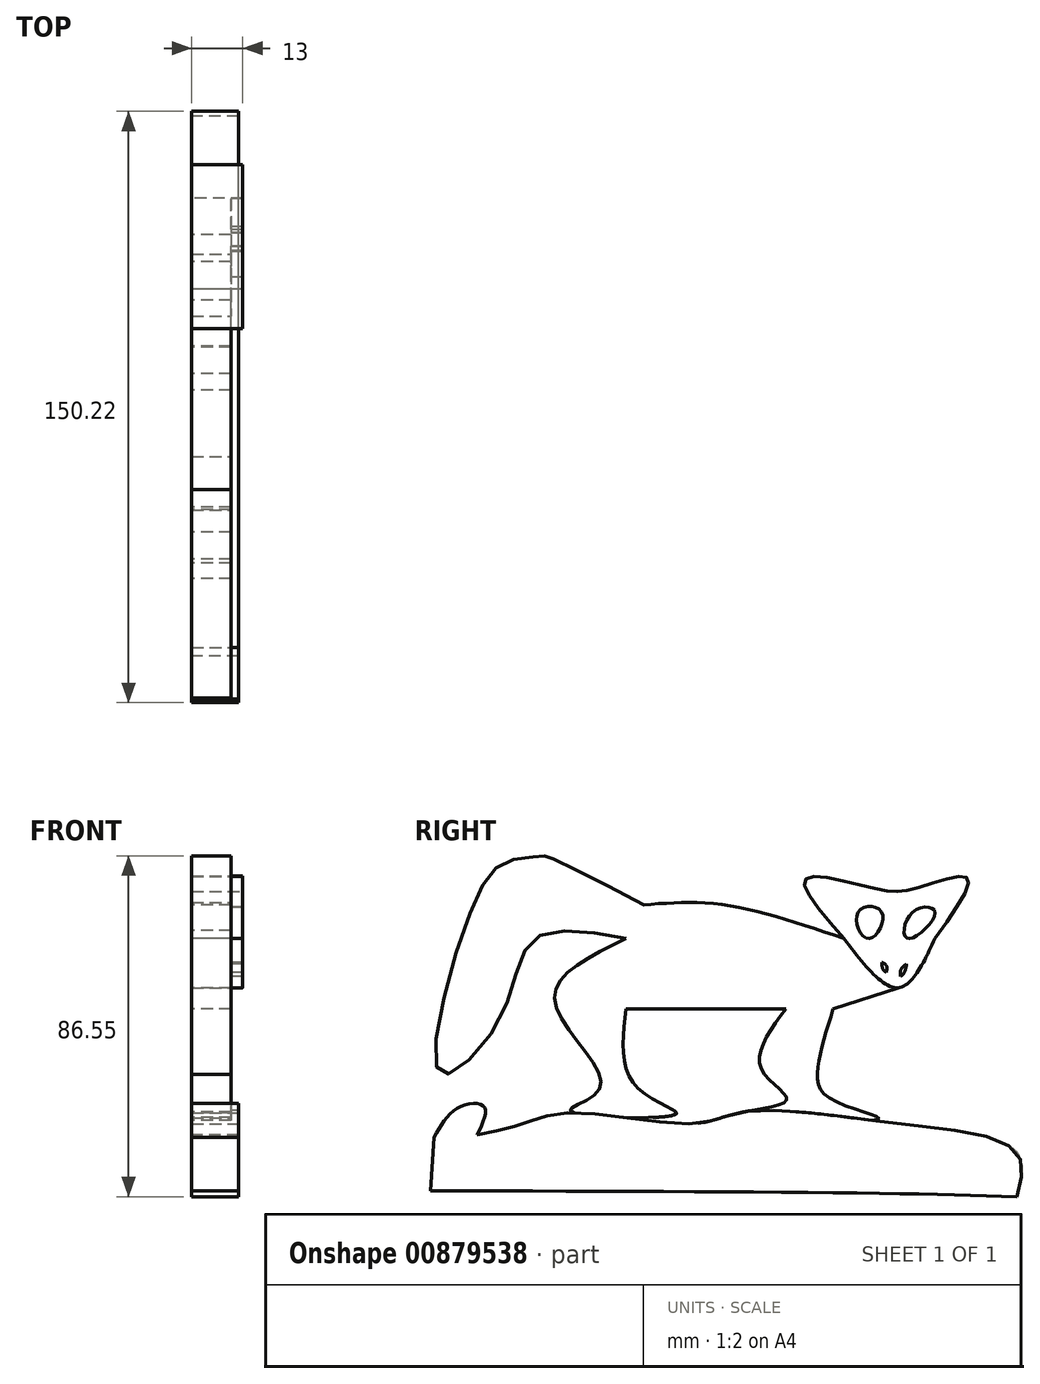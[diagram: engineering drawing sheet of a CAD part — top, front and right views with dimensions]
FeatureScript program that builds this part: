
annotation { "Feature Type Name" : "Feature", "Feature Type Description" : "" }
export const myFeature = defineFeature(function(context is Context, id is Id, definition is map)
    precondition{}
    {
        {
            var Q0;
            Q0=qCreatedBy(makeId("Right.planeOp"),FACE);
            var sketch = newSketch(context, id + "F0", { "sketchPlane" : qUnion([Q0])});
            skFitSpline(sketch, "E0", {"points": [v(-20.3, 8.57) * mm, v(-44.97, 20.9) * mm, v(-45.87, 20.9) * mm, v(-54.6, 19.7) * mm, v(-64.82, 5.56) * mm, v(-72.04, -34.14) * mm, v(-56.7, -20) * mm, v(-47.98, 0) * mm, v(-24.82, 0) * mm], "startDerivative": vector(-211.97, 110.73) * mm, "endDerivative": vector(178.69, -36.3) * mm});
            skFitSpline(sketch, "E1", {"points": [v(-24.82, 0) * mm, v(-42.86, -16.1) * mm, v(-31.43, -38.05) * mm, v(-38.95, -43.76) * mm, v(-12.18, -44.67) * mm, v(-21.8, -38.05) * mm, v(-24.82, -17.9) * mm], "startDerivative": vector(-149.38, -72.74) * mm, "endDerivative": vector(12.7, 128.41) * mm});
            skFitSpline(sketch, "E2", {"points": [v(-20.3, 8.57) * mm, v(0, 8.57) * mm, v(30.53, 0) * mm], "startDerivative": vector(43.61, 3.43) * mm, "endDerivative": vector(57.54, -19.72) * mm});
            skFitSpline(sketch, "E3", {"points": [v(-24.82, -17.9) * mm, v(-15.8, -17.9) * mm, v(3.76, -17.9) * mm, v(15.8, -17.9) * mm], "startDerivative": vector(28.68, 0) * mm, "endDerivative": vector(34.2, 0) * mm});
            skFitSpline(sketch, "E4", {"points": [v(15.8, -17.9) * mm, v(9.78, -33.54) * mm, v(15.8, -41.36) * mm, v(4.36, -44.37) * mm, v(39.25, -45.87) * mm, v(27.22, -40.76) * mm, v(23.91, -32.94) * mm, v(27.82, -17.9) * mm], "startDerivative": vector(-83.07, -110.92) * mm, "endDerivative": vector(34.72, 110.67) * mm});
            skFitSpline(sketch, "E5", {"points": [v(30.53, 0) * mm, v(20.9, 15.19) * mm, v(38.05, 12.78) * mm, v(48.88, 12.78) * mm, v(61.81, 15.5) * mm, v(53.7, 0) * mm], "startDerivative": vector(-80.15, 92.19) * mm, "endDerivative": vector(-69.87, -97.65) * mm});
            skFitSpline(sketch, "E6", {"points": [v(53.7, 0) * mm, v(44.37, -12.48) * mm, v(30.53, 0) * mm], "startDerivative": vector(-17.86, -38.08) * mm, "endDerivative": vector(-28.3, 36.96) * mm});
            skFitSpline(sketch, "E7", {"points": [v(44.37, -12.48) * mm, v(27.82, -17.9) * mm], "startDerivative": vector(-16.54, -5.41) * mm, "endDerivative": vector(-16.54, -5.41) * mm});
            skFitSpline(sketch, "E8", {"points": [v(34.14, 6.68) * mm, v(36.85, 0) * mm, v(40.16, 6.68) * mm, v(34.14, 6.68) * mm]});
            skFitSpline(sketch, "E9", {"points": [v(47.98, 6.68) * mm, v(46.77, 0) * mm, v(53.7, 6.68) * mm, v(47.98, 6.68) * mm]});
            skFitSpline(sketch, "E10", {"points": [v(40.16, -6.06) * mm, v(41.36, -8.57) * mm], "startDerivative": vector(1.2, -2.5) * mm, "endDerivative": vector(1.2, -2.5) * mm});
            skFitSpline(sketch, "E11", {"points": [v(46.47, -6.47) * mm, v(44.97, -9.17) * mm], "startDerivative": vector(-1.5, -2.7) * mm, "endDerivative": vector(-1.5, -2.7) * mm});
            skFitSpline(sketch, "E12", {"points": [v(40.16, -6.06) * mm, v(41.34, -6.9) * mm, v(41.36, -8.57) * mm], "startDerivative": vector(3.05, -1.37) * mm, "endDerivative": vector(-0.6, -3.62) * mm});
            skFitSpline(sketch, "E13", {"points": [v(46.47, -6.47) * mm, v(45.07, -7.74) * mm, v(44.97, -9.6) * mm], "startDerivative": vector(-3.45, -2.23) * mm, "endDerivative": vector(0.44, -4.06) * mm});
            skFitSpline(sketch, "E14", {"points": [v(46.47, -6.47) * mm, v(45.91, -8.57) * mm, v(44.97, -9.6) * mm], "startDerivative": vector(-0.7, -4.2) * mm, "endDerivative": vector(-2.37, -2) * mm});
            skFitSpline(sketch, "E15", {"points": [v(40.16, -6.06) * mm, v(40.56, -7.95) * mm, v(41.36, -8.57) * mm], "startDerivative": vector(0.34, -3.77) * mm, "endDerivative": vector(2.16, -1.11) * mm});
            skSolve(sketch);
        }
        {
            var Q0;
            Q0=makeQuery(id+"F0.imprint","IMPRINT",FACE,{"disambiguationData":[TD([[makeQuery(id+"F0.imprint","IMPRINT",EDGE,{"derivedFrom":sQuery(id+"F0.wireOp",EDGE,"E0")}),1.0]])]});
            extrude(context, id + "F1", {"entities" : qUnion([Q0]), "depth" : 10 * mm, "offsetDistance" : 25.4 * mm});
        }
        {
            var Q0;
            {var subQ1=sQuery(id+"F0.wireOp",EDGE,"E5");Q0=makeQuery(id+"F0.imprint","IMPRINT",FACE,{"disambiguationData":[TD([[makeQuery(id+"F0.imprint","IMPRINT",EDGE,{"derivedFrom":subQ1}),-1.0]])]});}
            extrude(context, id + "F2", {"entities" : qUnion([Q0]), "depth" : 13 * mm, "offsetDistance" : 25 * mm});
        }
        {
            var Q0;
            Q0=makeQuery(id+"F0.imprint","IMPRINT",FACE,{"disambiguationData":[TD([[makeQuery(id+"F0.imprint","IMPRINT",EDGE,{"derivedFrom":sQuery(id+"F0.wireOp",EDGE,"E8")}),1.0]])]});
            var Q1;
            Q1=makeQuery(id+"F0.imprint","IMPRINT",FACE,{"disambiguationData":[TD([[makeQuery(id+"F0.imprint","IMPRINT",EDGE,{"derivedFrom":sQuery(id+"F0.wireOp",EDGE,"E9")}),1.0]])]});
            extrude(context, id + "F3", {"entities" : qUnion([Q0, Q1]), "operationType" : NewBodyOperationType.ADD, "depth" : 10 * mm, "offsetDistance" : 25 * mm});
        }
        {
            var Q0;
            Q0=qCreatedBy(makeId("Right.planeOp"),FACE);
            var sketch = newSketch(context, id + "F4", { "sketchPlane" : qUnion([Q0])});
            skFitSpline(sketch, "E16", {"points": [v(-74.46, -64.1) * mm, v(37.15, -64.69) * mm, v(74.46, -65.58) * mm], "startDerivative": vector(199.7, -0.46) * mm, "endDerivative": vector(88.2, -2.7) * mm});
            skFitSpline(sketch, "E17", {"points": [v(-73.57, -50.48) * mm, v(-67.06, -42.78) * mm, v(-60.84, -42.78) * mm, v(-62.62, -49.88) * mm], "startDerivative": vector(14.21, 24.75) * mm, "endDerivative": vector(-12.97, -26.8) * mm});
            skFitSpline(sketch, "E18", {"points": [v(-62.62, -49.88) * mm, v(-50.77, -47) * mm, v(-39.23, -44.26) * mm, v(-7.55, -47) * mm, v(5.48, -43.96) * mm, v(44.26, -47) * mm, v(74.46, -54.33) * mm, v(74.46, -65.58) * mm], "startDerivative": vector(112.21, 23.12) * mm, "endDerivative": vector(-31.64, -117.94) * mm});
            skFitSpline(sketch, "E19", {"points": [v(-73.57, -50.48) * mm, v(-74.46, -64.1) * mm], "startDerivative": vector(-0.89, -13.62) * mm, "endDerivative": vector(-0.89, -13.62) * mm});
            skSolve(sketch);
        }
        {
            var Q0;
            Q0=makeQuery(id+"F4.imprint","IMPRINT",FACE,{"disambiguationData":[TD([[makeQuery(id+"F4.imprint","IMPRINT",EDGE,{"derivedFrom":sQuery(id+"F4.wireOp",EDGE,"E16")}),1.0]])]});
            extrude(context, id + "F5", {"entities" : qUnion([Q0]), "operationType" : NewBodyOperationType.ADD, "depth" : 12 * mm, "offsetDistance" : 25 * mm});
        }
        {
            var Q0;
            Q0=makeQuery(id+"F0.imprint","IMPRINT",FACE,{"disambiguationData":[TD([[makeQuery(id+"F0.imprint","IMPRINT",EDGE,{"derivedFrom":sQuery(id+"F0.wireOp",EDGE,"E10")}),1.0]])]});
            var Q1;
            Q1=makeQuery(id+"F0.imprint","IMPRINT",FACE,{"disambiguationData":[TD([[makeQuery(id+"F0.imprint","IMPRINT",EDGE,{"derivedFrom":sQuery(id+"F0.wireOp",EDGE,"E10")}),-1.0]])]});
            var Q2;
            Q2=makeQuery(id+"F0.imprint","IMPRINT",FACE,{"disambiguationData":[TD([[makeQuery(id+"F0.imprint","IMPRINT",EDGE,{"derivedFrom":sQuery(id+"F0.wireOp",EDGE,"E13")}),1.0]])]});
            extrude(context, id + "F6", {"entities" : qUnion([Q0, Q1, Q2]), "operationType" : NewBodyOperationType.ADD, "depth" : 10 * mm, "offsetDistance" : 25 * mm});
        }
    });
